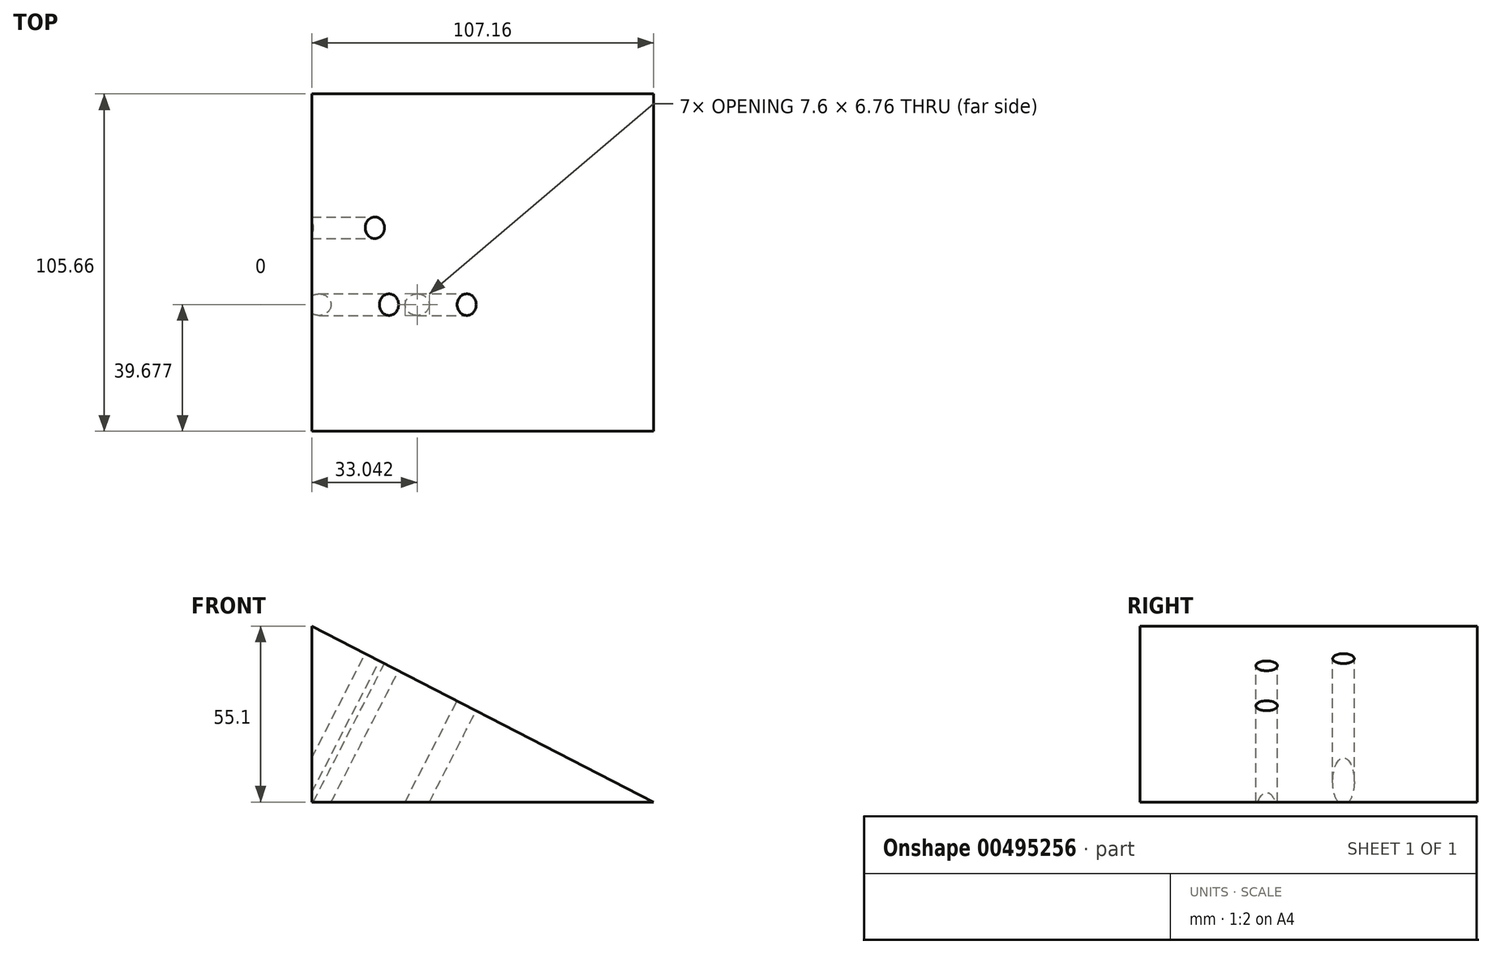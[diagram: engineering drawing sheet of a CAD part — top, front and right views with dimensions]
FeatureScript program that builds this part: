
annotation { "Feature Type Name" : "Feature", "Feature Type Description" : "" }
export const myFeature = defineFeature(function(context is Context, id is Id, definition is map)
    precondition{}
    {
        {
            var Q0;
            Q0=qCreatedBy(makeId("Front.planeOp"),FACE);
            var sketch = newSketch(context, id + "F0", { "sketchPlane" : qUnion([Q0])});
            skLineSegment(sketch, "E0", {"start": v(0, 0) * mm, "end": v(-107.16, 0) * mm});
            skLineSegment(sketch, "E1", {"start": v(-107.16, 0) * mm, "end": v(-107.16, 55.1) * mm});
            skLineSegment(sketch, "E2", {"start": v(-107.16, 55.1) * mm, "end": v(0, 0) * mm});
            skSolve(sketch);
        }
        {
            var Q0;
            Q0=makeQuery(id+"F0.imprint","IMPRINT",FACE,{"disambiguationData":[TD([[makeQuery(id+"F0.imprint","IMPRINT",EDGE,{"derivedFrom":sQuery(id+"F0.wireOp",EDGE,"E0")}),-1.0]])]});
            extrude(context, id + "F1", {"entities" : qUnion([Q0]), "endBound" : BoundingType.SYMMETRIC, "depth" : 105.66 * mm});
        }
        {
            var Q0;
            Q0=makeQuery(id+"F1.opExtrude","SWEPT_FACE",FACE,{"disambiguationData":[OSD([sQuery(id+"F0.wireOp",EDGE,"E2")])]});
            var sketch = newSketch(context, id + "F2", { "sketchPlane" : qUnion([Q0])});
            skPoint(sketch, "E3", {"position": v(-93.28, -13.15) * mm});
            skPoint(sketch, "E4", {"position": v(-98.25, 10.95) * mm});
            skPoint(sketch, "E5", {"position": v(-65.91, -13.15) * mm});
            skSolve(sketch);
        }
        {
            var Q0;
            Q0=sQuery(id+"F2.wireOp",VERTEX,"E4");
            var Q1;
            Q1=sQuery(id+"F2.wireOp",VERTEX,"E3");
            var Q2;
            Q2=sQuery(id+"F2.wireOp",VERTEX,"E5");
            var Q3;
            Q3=makeQuery(id+"F1.opExtrude","SWEPT_BODY",BODY,{"disambiguationData":[OSD([sQuery(id+"F0.wireOp",EDGE,"E0"),sQuery(id+"F0.wireOp",EDGE,"E1"),sQuery(id+"F0.wireOp",EDGE,"E2")])]});
            hole(context, id + "F3", {"style" : HoleStyle.SIMPLE, "endStyle" : HoleEndStyle.THROUGH, "standardTappedOrClearance" : lookupTablePath({ "standard" : "ANSI", "fit" : "Normal (ASME)", "size" : "1/4", "type" : "Clearance" }), "standardBlindInLast" : lookupTablePath({ "fit" : "Free", "standard" : "ANSI", "size" : "1/4", "type" : "Clearance" }), "holeDiameter" : 6.76 * mm, "isTappedThrough" : true, "tappedDepth" : 12.7 * mm, "tapClearance" : 3, "locations" : qUnion([Q0, Q1, Q2]), "scope" : qUnion([Q3])});
        }
    });
